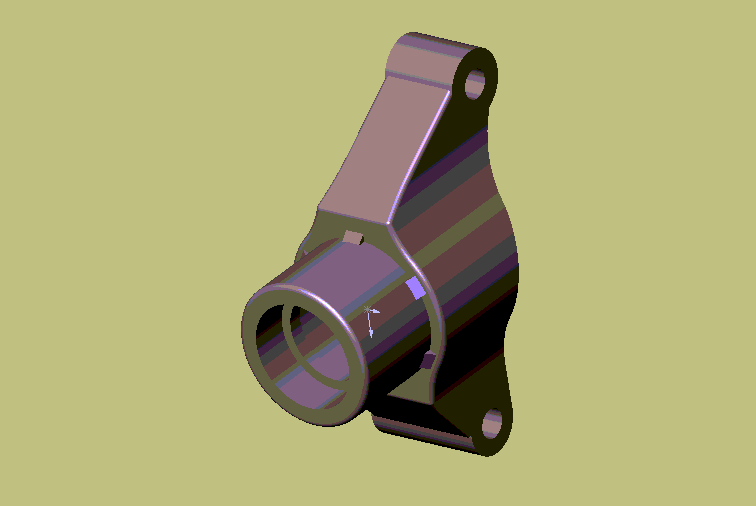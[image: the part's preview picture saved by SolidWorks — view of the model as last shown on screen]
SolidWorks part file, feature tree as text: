
SOLIDWORKS PART (.sldprt)
format: sldprt  version: not decoded by parser v0  size: 285,184 bytes
history: native  units: mm
features: sketch x9, cut_extrude x6, plane x3, extrude x3, material x1, pattern_circular x1, fillet x1 (+8 scaffold rows collapsed)
feature tree (32):
  scaffold x8  (default folders/planes/origin — collapsed)
  material  "Matériau <non spécifié>"
  plane  "Plane1"
  plane  "Plane2"
  plane  "Plane3"
  sketch  "Esquisse1"  dims[D1=18.0mm D4=10.0mm D7=10.0mm D2=12.0mm D3=22.0mm D5=8.0mm D6=22.0mm D8=~9.154767mm D9=~9.154767mm]
  extrude  "Base-Extrusion"  Depth=20mm
  sketch  "Esquisse4"  dims[D1=15.0mm]
  extrude  "Boss.-Extru.1"  Depth=10mm
  sketch  "Esquisse5"  dims[D1=11.0mm]
  cut_extrude  "Enlèv. mat.-Extru.2"  Depth=4mm
  sketch  "Esquisse9"  dims[D1=9.0mm]
  cut_extrude  "Enlèv. mat.-Extru.6"  Depth=1.5mm
  sketch  "Esquisse10"  dims[D1=11.0mm]
  cut_extrude  "Enlèv. mat.-Extru.7"  Depth=4mm
  sketch  "Esquisse11"  dims[D1=14.0mm]
  cut_extrude  "Enlèv. mat.-Extru.8"  [1 undecoded]
  sketch  "Esquisse13"  dims[D1=1.25mm D2=1.25mm]
  extrude  "Boss.-Extru.2"  Depth=2mm
  pattern_circular  "Répétition circulaire3"  Count=6 Angle=60deg
  sketch  "Esquisse15"  dims[D7=30.0mm D8=3.5mm D1=8.0mm D2=15.5mm D3=15.0mm D4=17.0mm D5=19.0mm D6=10.0mm D9=17.0mm D10=18.0mm]
  cut_extrude  "Enlèv. mat.-Extru.10"  Depth=52mm
  sketch  "Esquisse16"  dims[D1=3.0mm D2=3.0mm]
  cut_extrude  "Enlèv. mat.-Extru.11"  [1 undecoded]
  fillet  "Congé2"  Radius=0.5mm
decode coverage: 18 of 20 modeling features carry decoded parameters
note: ~ marks probable driven/reference dimensions
note: 2 parameter values undecoded
note: suppression state not decoded; provenance and decode notes live in map.json
